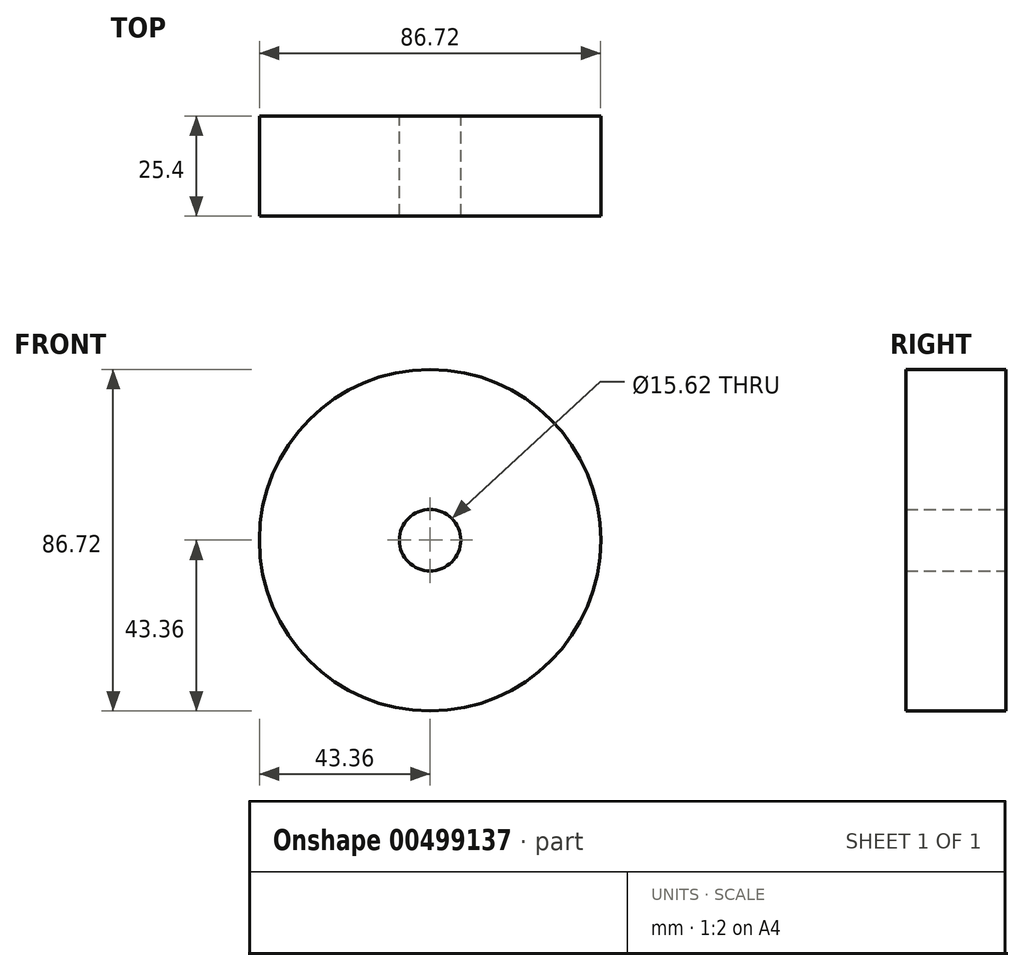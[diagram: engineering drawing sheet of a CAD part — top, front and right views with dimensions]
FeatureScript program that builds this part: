
annotation { "Feature Type Name" : "Feature", "Feature Type Description" : "" }
export const myFeature = defineFeature(function(context is Context, id is Id, definition is map)
    precondition{}
    {
        {
            var Q0;
            Q0=qCreatedBy(makeId("Front.planeOp"),FACE);
            var sketch = newSketch(context, id + "F0", { "sketchPlane" : qUnion([Q0])});
            skCircle(sketch, "E0", {"center": v(0, 0) * mm, "radius": 43.36 * mm});
            skCircle(sketch, "E1", {"center": v(0, 0) * mm, "radius": 29.5 * mm});
            skCircle(sketch, "E2", {"center": v(0, 0) * mm, "radius": 16.78 * mm});
            skCircle(sketch, "E3", {"center": v(0, 0) * mm, "radius": 7.8 * mm});
            skSolve(sketch);
        }
        {
            var Q0;
            Q0 = qSketchRegion(id + "F0", true);
            var Q1;
            Q1=makeQuery(id+"F0.imprint","IMPRINT",FACE,{"disambiguationData":[TD([[makeQuery(id+"F0.imprint","IMPRINT",EDGE,{"derivedFrom":sQuery(id+"F0.wireOp",EDGE,"E1")}),1.0]])]});
            var Q2;
            Q2=makeQuery(id+"F0.imprint","IMPRINT",FACE,{"disambiguationData":[TD([[makeQuery(id+"F0.imprint","IMPRINT",EDGE,{"derivedFrom":sQuery(id+"F0.wireOp",EDGE,"E2")}),1.0]])]});
            extrude(context, id + "F1", {"entities" : qUnion([Q0, Q1, Q2]), "depth" : 25.4 * mm});
        }
    });
